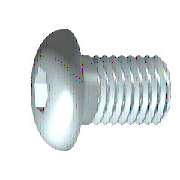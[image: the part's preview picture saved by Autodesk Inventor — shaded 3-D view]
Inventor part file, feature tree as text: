
AUTODESK INVENTOR PART (.ipt)
format: ipt  version: 2023.4 (Build 274418000, 418)  size: 193,536 bytes
history: native  units: mm (DEFAULTED — no unit token found)
features: extrude x1, plane x1, fillet x1
ambient origin geometry x7: Origin, YZ Plane, XY Plane, X Axis, Y Axis, Z Axis, Center Point
bodies: Solid1 (feature_tree), Body (feature_tree)
feature tree (3):
  extrude  "Slot"  Depth=10.6678mm
  plane  "Work Plane1"
  fillet  "Fillet2"  Radius=2.0321mm
